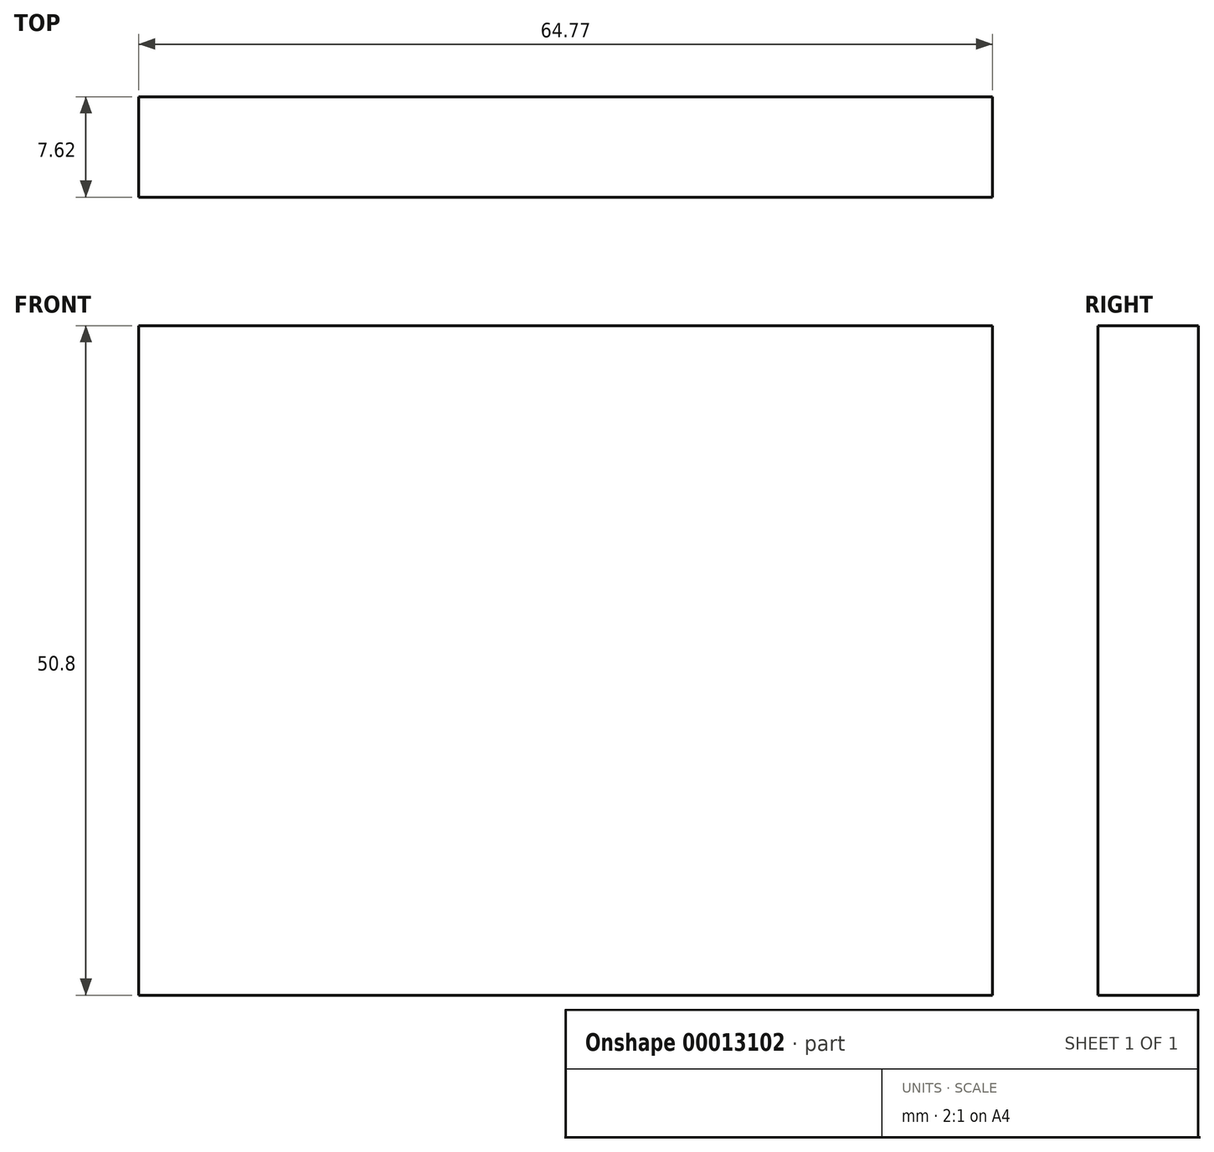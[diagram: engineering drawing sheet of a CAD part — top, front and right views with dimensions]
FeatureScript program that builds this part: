
annotation { "Feature Type Name" : "Feature", "Feature Type Description" : "" }
export const myFeature = defineFeature(function(context is Context, id is Id, definition is map)
    precondition{}
    {
        {
            var Q0;
            Q0=qCreatedBy(makeId("Front.planeOp"),FACE);
            var sketch = newSketch(context, id + "F0", { "sketchPlane" : qUnion([Q0])});
            skLineSegment(sketch, "E0.bottom", {"start": v(-40.8, 13.57) * mm, "end": v(23.98, 13.57) * mm});
            skLineSegment(sketch, "E0.top", {"start": v(-40.8, -37.23) * mm, "end": v(23.98, -37.23) * mm});
            skLineSegment(sketch, "E0.left", {"start": v(-40.8, 13.57) * mm, "end": v(-40.8, -37.23) * mm});
            skLineSegment(sketch, "E0.right", {"start": v(23.98, 13.57) * mm, "end": v(23.98, -37.23) * mm});
            skSolve(sketch);
        }
        {
            var Q0;
            Q0=makeQuery(id+"F0.imprint","IMPRINT",FACE,{"disambiguationData":[TD([[makeQuery(id+"F0.imprint","IMPRINT",EDGE,{"derivedFrom":sQuery(id+"F0.wireOp",EDGE,"E0.bottom")}),-1.0]])]});
            extrude(context, id + "F1", {"entities" : qUnion([Q0]), "depth" : 7.62 * mm, "offsetDistance" : 25.4 * mm});
        }
    });
